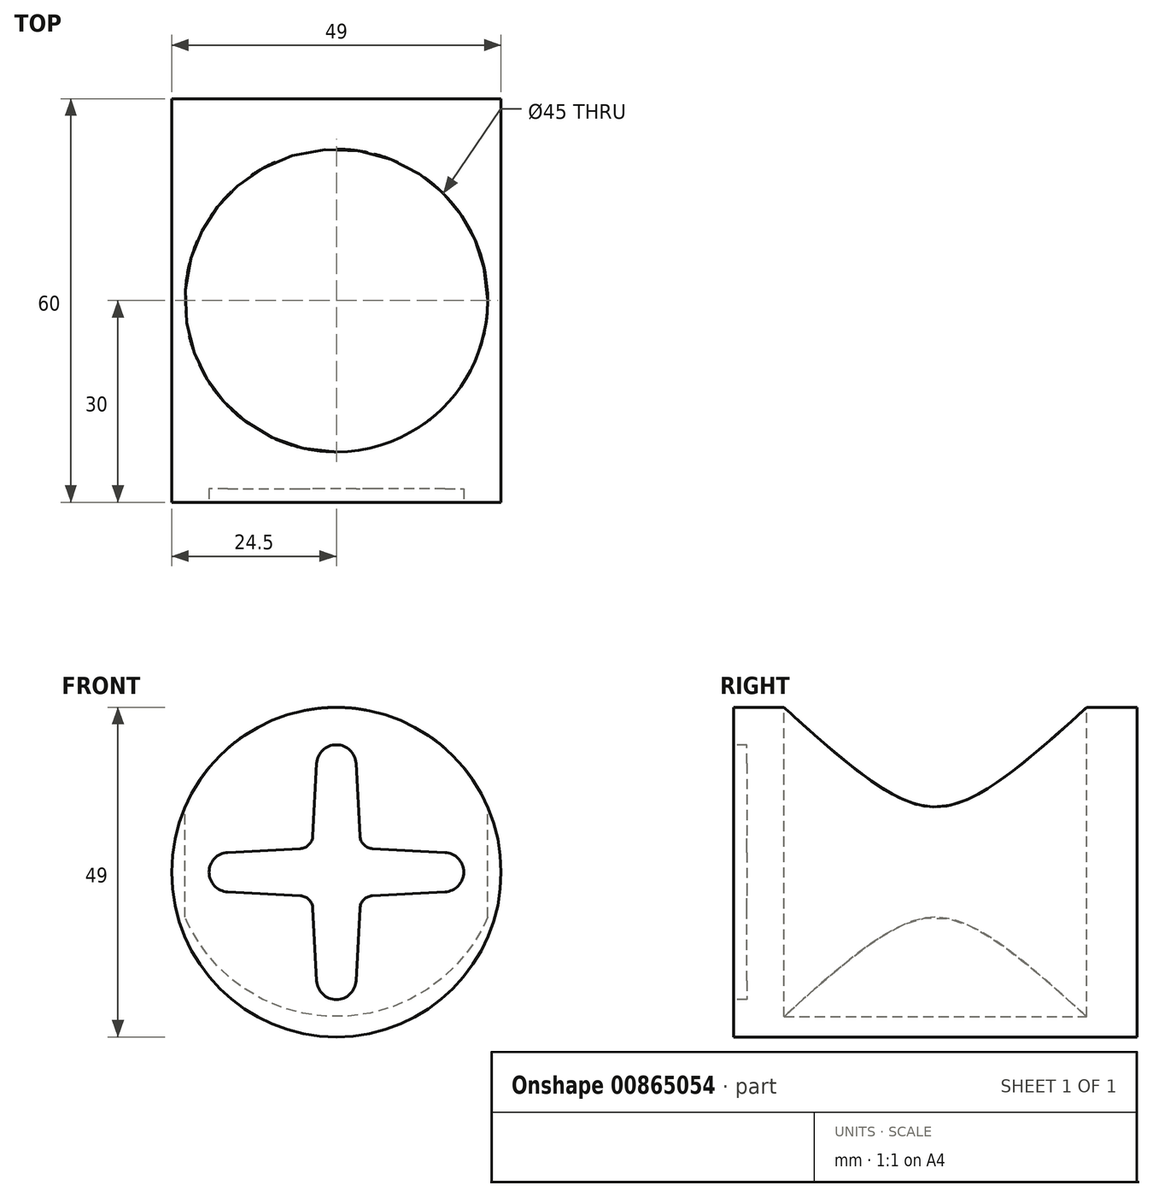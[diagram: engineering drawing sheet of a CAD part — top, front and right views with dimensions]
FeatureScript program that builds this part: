
annotation { "Feature Type Name" : "Feature", "Feature Type Description" : "" }
export const myFeature = defineFeature(function(context is Context, id is Id, definition is map)
    precondition{}
    {
        {
            var Q0;
            Q0=qCreatedBy(makeId("Front.planeOp"),FACE);
            var sketch = newSketch(context, id + "F0", { "sketchPlane" : qUnion([Q0])});
            skCircle(sketch, "E0", {"center": v(0, 0) * mm, "radius": 24.5 * mm});
            skSolve(sketch);
        }
        {
            var Q0;
            Q0 = qSketchRegion(id + "F0", true);
            extrude(context, id + "F1", {"entities" : qUnion([Q0]), "endBound" : BoundingType.SYMMETRIC, "depth" : 60 * mm, "offsetDistance" : 25 * mm});
        }
        {
            var Q0;
            Q0=qCreatedBy(makeId("Top.planeOp"),FACE);
            var sketch = newSketch(context, id + "F2", { "sketchPlane" : qUnion([Q0])});
            skCircle(sketch, "E1", {"center": v(0, 0) * mm, "radius": 22.5 * mm});
            skSolve(sketch);
        }
        {
            var Q0;
            Q0 = qSketchRegion(id + "F2", true);
            var Q1;
            Q1=makeQuery(id+"F1.opExtrude","SWEPT_FACE",FACE,{"disambiguationData":[OSD([sQuery(id+"F0.wireOp",EDGE,"E0")])]});
            extrude(context, id + "F3", {"entities" : qUnion([Q0]), "operationType" : NewBodyOperationType.REMOVE, "endBound" : BoundingType.UP_TO_SURFACE, "oppositeDirection" : true, "depth" : 25 * mm, "endBoundEntityFace" : qUnion([Q1]), "hasOffset" : true, "offsetDistance" : 3 * mm});
        }
        {
            var Q0;
            Q0 = qSketchRegion(id + "F2", true);
            extrude(context, id + "F4", {"entities" : qUnion([Q0]), "operationType" : NewBodyOperationType.REMOVE, "depth" : 25 * mm, "offsetDistance" : 25 * mm});
        }
        {
            var Q0;
            Q0=makeQuery(id+"F1.opExtrude","CAP_FACE",FACE,{"disambiguationData":[OSD([sQuery(id+"F0.wireOp",EDGE,"E0")])],"isStart":false});
            var sketch = newSketch(context, id + "F5", { "sketchPlane" : qUnion([Q0])});
            skLineSegment(sketch, "E2", {"start": v(0, 0) * mm, "end": v(0, 41.54) * mm, "construction": true});
            skLineSegment(sketch, "E3", {"start": v(0, 0) * mm, "end": v(41.18, 0) * mm, "construction": true});
            skLineSegment(sketch, "E4", {"start": v(2.94, 16.15) * mm, "end": v(3.5, 5.4) * mm});
            skArc(sketch, "E5", {"start": v(2.94, 16.15) * mm, "mid": v(2.02, 18.13) * mm, "end": v(0, 18.94) * mm});
            skLineSegment(sketch, "E6", {"start": v(0, 0) * mm, "end": v(39.17, 39.17) * mm, "construction": true});
            skArc(sketch, "E7", {"start": v(3.5, 5.4) * mm, "mid": v(3.67, 4.68) * mm, "end": v(4.08, 4.08) * mm});
            skArc(sketch, "E8.MirrorCS", {"start": v(5.4, 3.5) * mm, "mid": v(4.68, 3.67) * mm, "end": v(4.08, 4.08) * mm});
            skLineSegment(sketch, "E9.MirrorCS", {"start": v(16.15, 2.94) * mm, "end": v(5.4, 3.5) * mm});
            skArc(sketch, "E10.MirrorCS", {"start": v(16.15, 2.94) * mm, "mid": v(18.13, 2.02) * mm, "end": v(18.94, 0) * mm});
            skArc(sketch, "E11.MirrorCS", {"start": v(-3.5, 5.4) * mm, "mid": v(-3.67, 4.68) * mm, "end": v(-4.08, 4.08) * mm});
            skArc(sketch, "E12.MirrorCS", {"start": v(-5.4, 3.5) * mm, "mid": v(-4.68, 3.67) * mm, "end": v(-4.08, 4.08) * mm});
            skArc(sketch, "E13.MirrorCS", {"start": v(-16.15, 2.94) * mm, "mid": v(-18.13, 2.02) * mm, "end": v(-18.94, 0) * mm});
            skLineSegment(sketch, "E14.MirrorCS", {"start": v(-2.94, 16.15) * mm, "end": v(-3.5, 5.4) * mm});
            skArc(sketch, "E15.MirrorCS", {"start": v(-2.94, 16.15) * mm, "mid": v(-2.02, 18.13) * mm, "end": v(0, 18.94) * mm});
            skLineSegment(sketch, "E16.MirrorCS", {"start": v(-16.15, 2.94) * mm, "end": v(-5.4, 3.5) * mm});
            skArc(sketch, "E17.MirrorCS", {"start": v(-3.5, -5.4) * mm, "mid": v(-3.67, -4.68) * mm, "end": v(-4.08, -4.08) * mm});
            skArc(sketch, "E18.MirrorCS", {"start": v(3.5, -5.4) * mm, "mid": v(3.67, -4.68) * mm, "end": v(4.08, -4.08) * mm});
            skArc(sketch, "E19.MirrorCS", {"start": v(5.4, -3.5) * mm, "mid": v(4.68, -3.67) * mm, "end": v(4.08, -4.08) * mm});
            skArc(sketch, "E20.MirrorCS", {"start": v(-5.4, -3.5) * mm, "mid": v(-4.68, -3.67) * mm, "end": v(-4.08, -4.08) * mm});
            skArc(sketch, "E21.MirrorCS", {"start": v(16.15, -2.94) * mm, "mid": v(18.13, -2.02) * mm, "end": v(18.94, 0) * mm});
            skArc(sketch, "E22.MirrorCS", {"start": v(2.94, -16.15) * mm, "mid": v(2.02, -18.13) * mm, "end": v(0, -18.94) * mm});
            skLineSegment(sketch, "E23.MirrorCS", {"start": v(-16.15, -2.94) * mm, "end": v(-5.4, -3.5) * mm});
            skLineSegment(sketch, "E24.MirrorCS", {"start": v(2.94, -16.15) * mm, "end": v(3.5, -5.4) * mm});
            skLineSegment(sketch, "E25.MirrorCS", {"start": v(16.15, -2.94) * mm, "end": v(5.4, -3.5) * mm});
            skArc(sketch, "E26.MirrorCS", {"start": v(-2.94, -16.15) * mm, "mid": v(-2.02, -18.13) * mm, "end": v(0, -18.94) * mm});
            skArc(sketch, "E27.MirrorCS", {"start": v(-16.15, -2.94) * mm, "mid": v(-18.13, -2.02) * mm, "end": v(-18.94, 0) * mm});
            skLineSegment(sketch, "E28.MirrorCS", {"start": v(-2.94, -16.15) * mm, "end": v(-3.5, -5.4) * mm});
            skSolve(sketch);
        }
        {
            var Q0;
            Q0 = qSketchRegion(id + "F5", true);
            extrude(context, id + "F6", {"entities" : qUnion([Q0]), "operationType" : NewBodyOperationType.REMOVE, "oppositeDirection" : true, "depth" : 2 * mm, "offsetDistance" : 25 * mm});
        }
    });
